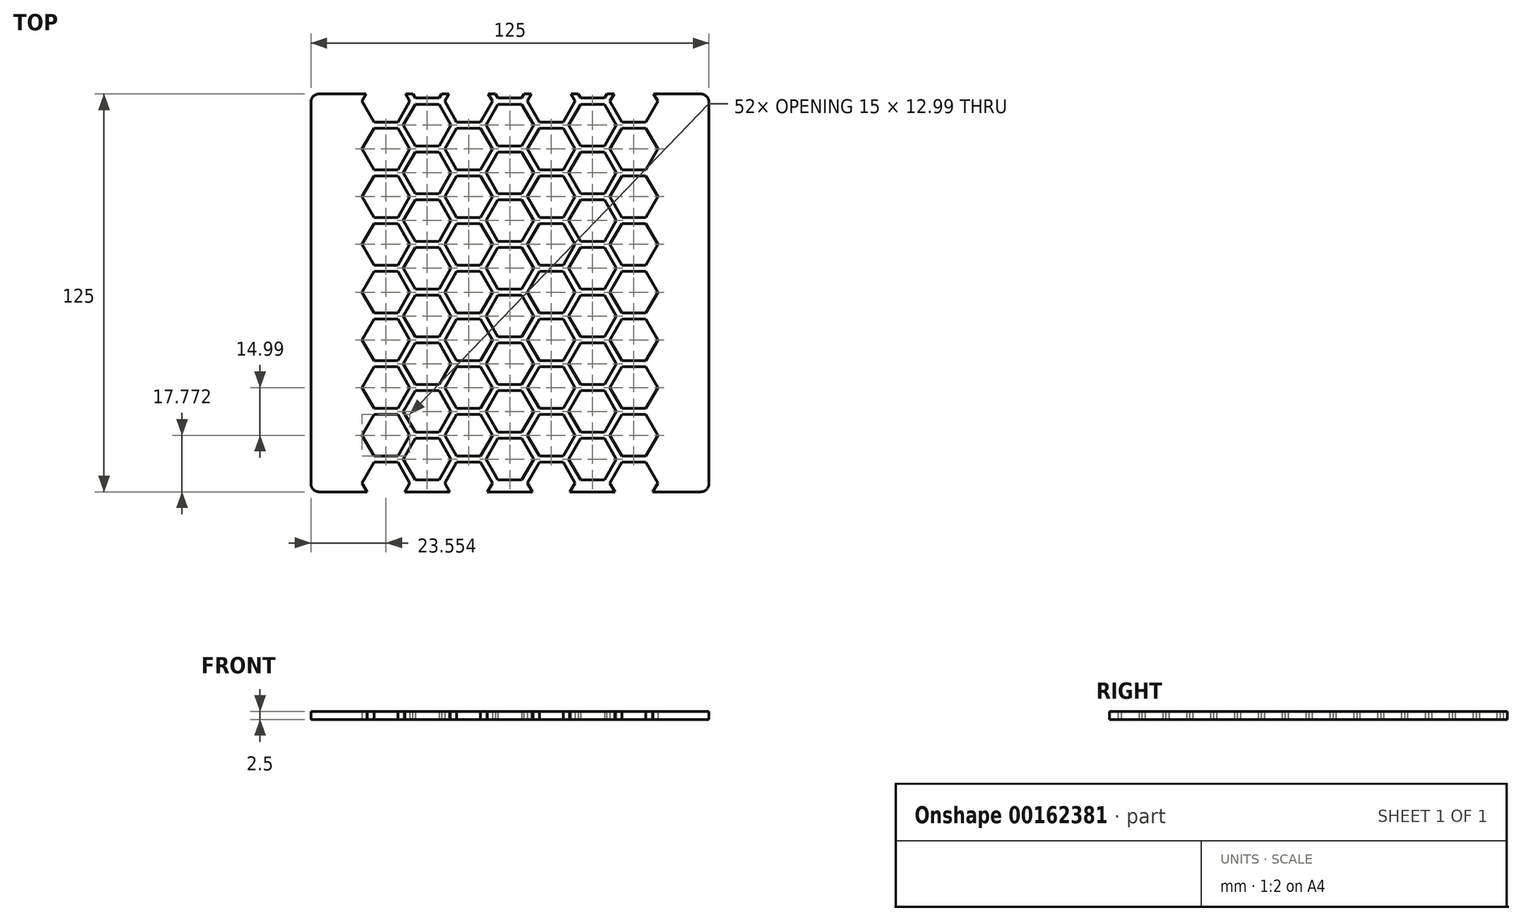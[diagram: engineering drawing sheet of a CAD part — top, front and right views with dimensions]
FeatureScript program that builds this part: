
annotation { "Feature Type Name" : "Feature", "Feature Type Description" : "" }
export const myFeature = defineFeature(function(context is Context, id is Id, definition is map)
    precondition{}
    {
        {
            var Q0;
            Q0=qCreatedBy(makeId("Top.planeOp"),FACE);
            var sketch = newSketch(context, id + "F0", { "sketchPlane" : qUnion([Q0])});
            skPoint(sketch, "E0.middle", {"position": v(0, 0) * mm});
            skLineSegment(sketch, "E1.bottom", {"start": v(60, 62.5) * mm, "end": v(-60, 62.5) * mm});
            skLineSegment(sketch, "E1.top", {"start": v(60, -62.5) * mm, "end": v(-60, -62.5) * mm});
            skLineSegment(sketch, "E1.left", {"start": v(62.5, 60) * mm, "end": v(62.5, -60) * mm});
            skLineSegment(sketch, "E1.right", {"start": v(-62.5, 60) * mm, "end": v(-62.5, -60) * mm});
            skArc(sketch, "E2", {"start": v(-60, 62.5) * mm, "mid": v(-61.77, 61.77) * mm, "end": v(-62.5, 60) * mm});
            skArc(sketch, "E3", {"start": v(62.5, 60) * mm, "mid": v(61.77, 61.77) * mm, "end": v(60, 62.5) * mm});
            skArc(sketch, "E4", {"start": v(60, -62.5) * mm, "mid": v(61.77, -61.77) * mm, "end": v(62.5, -60) * mm});
            skArc(sketch, "E5", {"start": v(-62.5, -60) * mm, "mid": v(-61.77, -61.77) * mm, "end": v(-60, -62.5) * mm});
            skLineSegment(sketch, "E6", {"start": v(0, 0) * mm, "end": v(0, 62.5) * mm, "construction": true});
            skLineSegment(sketch, "E7", {"start": v(0, 0) * mm, "end": v(0, -62.5) * mm, "construction": true});
            skSolve(sketch);
        }
        {
            var Q0;
            Q0=makeQuery(id+"F0.imprint","IMPRINT",FACE,{"disambiguationData":[TD([[makeQuery(id+"F0.imprint","IMPRINT",EDGE,{"derivedFrom":sQuery(id+"F0.wireOp",EDGE,"E1.bottom")}),1.0]])]});
            extrude(context, id + "F1", {"entities" : qUnion([Q0]), "offsetDistance" : 25 * mm, "depth" : 2.5 * mm});
        }
        {
            var Q0;
            Q0=qCreatedBy(makeId("Top.planeOp"),FACE);
            var sketch = newSketch(context, id + "F2", { "sketchPlane" : qUnion([Q0])});
            skCircle(sketch, "E8.cCircle", {"center": v(0, -52.22) * mm, "radius": 7.5 * mm, "construction": true});
            skLineSegment(sketch, "E8.0", {"start": v(7.5, -52.22) * mm, "end": v(3.75, -58.72) * mm});
            skLineSegment(sketch, "E8.1", {"start": v(3.75, -58.72) * mm, "end": v(-3.75, -58.72) * mm});
            skLineSegment(sketch, "E8.2", {"start": v(-3.75, -58.72) * mm, "end": v(-7.5, -52.22) * mm});
            skLineSegment(sketch, "E8.3", {"start": v(-7.5, -52.22) * mm, "end": v(-3.75, -45.73) * mm});
            skLineSegment(sketch, "E8.4", {"start": v(-3.75, -45.73) * mm, "end": v(3.75, -45.73) * mm});
            skLineSegment(sketch, "E8.5", {"start": v(3.75, -45.73) * mm, "end": v(7.5, -52.22) * mm});
            skCircle(sketch, "E9.cCircle", {"center": v(-12.98, -59.72) * mm, "radius": 7.5 * mm, "construction": true});
            skLineSegment(sketch, "E9.0", {"start": v(-16.73, -53.22) * mm, "end": v(-9.23, -53.22) * mm});
            skLineSegment(sketch, "E9.1", {"start": v(-9.23, -53.22) * mm, "end": v(-5.48, -59.72) * mm});
            skLineSegment(sketch, "E9.2", {"start": v(-5.48, -59.72) * mm, "end": v(-9.23, -66.21) * mm});
            skLineSegment(sketch, "E9.3", {"start": v(-9.23, -66.21) * mm, "end": v(-16.73, -66.21) * mm});
            skLineSegment(sketch, "E9.4", {"start": v(-16.73, -66.21) * mm, "end": v(-20.48, -59.72) * mm});
            skLineSegment(sketch, "E9.5", {"start": v(-20.48, -59.72) * mm, "end": v(-16.73, -53.22) * mm});
            skLineSegment(sketch, "E10", {"start": v(-12.98, -59.72) * mm, "end": v(0, -52.22) * mm, "construction": true});
            skCircle(sketch, "E11.MirrorC", {"center": v(12.98, -59.72) * mm, "radius": 7.5 * mm, "construction": true});
            skLineSegment(sketch, "E12.MirrorCS", {"start": v(5.48, -59.72) * mm, "end": v(9.23, -66.21) * mm});
            skLineSegment(sketch, "E13.MirrorCS", {"start": v(9.23, -66.21) * mm, "end": v(16.73, -66.21) * mm});
            skLineSegment(sketch, "E14.MirrorCS", {"start": v(16.73, -66.21) * mm, "end": v(20.48, -59.72) * mm});
            skLineSegment(sketch, "E15.MirrorCS", {"start": v(20.48, -59.72) * mm, "end": v(16.73, -53.22) * mm});
            skLineSegment(sketch, "E16.MirrorCS", {"start": v(16.73, -53.22) * mm, "end": v(9.23, -53.22) * mm});
            skLineSegment(sketch, "E17.MirrorCS", {"start": v(9.23, -53.22) * mm, "end": v(5.48, -59.72) * mm});
            skLineSegment(sketch, "E18.MirrorCS", {"start": v(12.98, -59.72) * mm, "end": v(0, -52.22) * mm, "construction": true});
            skLineSegment(sketch, "E19.1.0.0", {"start": v(38.95, -59.72) * mm, "end": v(25.96, -52.22) * mm, "construction": true});
            skLineSegment(sketch, "E19.1.0.1", {"start": v(29.71, -45.73) * mm, "end": v(33.46, -52.22) * mm});
            skLineSegment(sketch, "E19.1.0.2", {"start": v(12.98, -59.72) * mm, "end": v(25.96, -52.22) * mm, "construction": true});
            skLineSegment(sketch, "E19.1.0.3", {"start": v(22.21, -45.73) * mm, "end": v(29.71, -45.73) * mm});
            skLineSegment(sketch, "E19.1.0.4", {"start": v(42.7, -66.21) * mm, "end": v(46.45, -59.72) * mm});
            skLineSegment(sketch, "E19.1.0.5", {"start": v(46.45, -59.72) * mm, "end": v(42.7, -53.22) * mm});
            skLineSegment(sketch, "E19.1.0.6", {"start": v(31.45, -59.72) * mm, "end": v(35.2, -66.21) * mm});
            skCircle(sketch, "E19.1.0.7", {"center": v(25.96, -52.22) * mm, "radius": 7.5 * mm, "construction": true});
            skLineSegment(sketch, "E19.1.0.8", {"start": v(35.2, -53.22) * mm, "end": v(31.45, -59.72) * mm});
            skLineSegment(sketch, "E19.1.0.9", {"start": v(33.46, -52.22) * mm, "end": v(29.71, -58.72) * mm});
            skLineSegment(sketch, "E19.1.0.10", {"start": v(35.2, -66.21) * mm, "end": v(42.7, -66.21) * mm});
            skLineSegment(sketch, "E19.1.0.11", {"start": v(29.71, -58.72) * mm, "end": v(22.21, -58.72) * mm});
            skLineSegment(sketch, "E19.1.0.12", {"start": v(22.21, -58.72) * mm, "end": v(18.46, -52.22) * mm});
            skLineSegment(sketch, "E19.1.0.13", {"start": v(42.7, -53.22) * mm, "end": v(35.2, -53.22) * mm});
            skLineSegment(sketch, "E19.1.0.14", {"start": v(18.46, -52.22) * mm, "end": v(22.21, -45.73) * mm});
            skCircle(sketch, "E19.1.0.15", {"center": v(38.95, -59.72) * mm, "radius": 7.5 * mm, "construction": true});
            skLineSegment(sketch, "E19.direction1", {"start": v(-12.98, -59.72) * mm, "end": v(12.98, -59.72) * mm, "construction": true});
            skCircle(sketch, "E20.MirrorC", {"center": v(-25.96, -52.22) * mm, "radius": 7.5 * mm, "construction": true});
            skLineSegment(sketch, "E21.MirrorCS", {"start": v(-35.2, -66.21) * mm, "end": v(-42.7, -66.21) * mm});
            skLineSegment(sketch, "E22.MirrorCS", {"start": v(-12.98, -59.72) * mm, "end": v(-25.96, -52.22) * mm, "construction": true});
            skLineSegment(sketch, "E23.MirrorCS", {"start": v(-38.95, -59.72) * mm, "end": v(-25.96, -52.22) * mm, "construction": true});
            skLineSegment(sketch, "E24.MirrorCS", {"start": v(-46.45, -59.72) * mm, "end": v(-42.7, -53.22) * mm});
            skCircle(sketch, "E25.MirrorC", {"center": v(-38.95, -59.72) * mm, "radius": 7.5 * mm, "construction": true});
            skLineSegment(sketch, "E26.MirrorCS", {"start": v(-35.2, -53.22) * mm, "end": v(-31.45, -59.72) * mm});
            skLineSegment(sketch, "E27.MirrorCS", {"start": v(-29.71, -58.72) * mm, "end": v(-22.21, -58.72) * mm});
            skLineSegment(sketch, "E28.MirrorCS", {"start": v(-22.21, -45.73) * mm, "end": v(-29.71, -45.73) * mm});
            skLineSegment(sketch, "E29.MirrorCS", {"start": v(-22.21, -58.72) * mm, "end": v(-18.46, -52.22) * mm});
            skLineSegment(sketch, "E30.MirrorCS", {"start": v(-18.46, -52.22) * mm, "end": v(-22.21, -45.73) * mm});
            skLineSegment(sketch, "E31.MirrorCS", {"start": v(-31.45, -59.72) * mm, "end": v(-35.2, -66.21) * mm});
            skLineSegment(sketch, "E32.MirrorCS", {"start": v(-42.7, -66.21) * mm, "end": v(-46.45, -59.72) * mm});
            skLineSegment(sketch, "E33.MirrorCS", {"start": v(-33.46, -52.22) * mm, "end": v(-29.71, -58.72) * mm});
            skLineSegment(sketch, "E34.MirrorCS", {"start": v(-29.71, -45.73) * mm, "end": v(-33.46, -52.22) * mm});
            skLineSegment(sketch, "E35.MirrorCS", {"start": v(-42.7, -53.22) * mm, "end": v(-35.2, -53.22) * mm});
            skLineSegment(sketch, "E36.0.1.0", {"start": v(-3.75, -30.74) * mm, "end": v(3.75, -30.74) * mm});
            skLineSegment(sketch, "E36.0.1.1", {"start": v(-7.5, -37.23) * mm, "end": v(-3.75, -30.74) * mm});
            skLineSegment(sketch, "E36.0.1.2", {"start": v(7.5, -37.23) * mm, "end": v(3.75, -43.73) * mm});
            skLineSegment(sketch, "E36.0.1.3", {"start": v(-20.48, -44.73) * mm, "end": v(-16.73, -38.23) * mm});
            skCircle(sketch, "E36.0.1.4", {"center": v(-25.96, -37.23) * mm, "radius": 7.5 * mm, "construction": true});
            skLineSegment(sketch, "E36.0.1.5", {"start": v(35.2, -38.23) * mm, "end": v(31.45, -44.73) * mm});
            skLineSegment(sketch, "E36.0.1.6", {"start": v(12.98, -44.73) * mm, "end": v(0, -37.23) * mm, "construction": true});
            skCircle(sketch, "E36.0.1.7", {"center": v(38.95, -44.73) * mm, "radius": 7.5 * mm, "construction": true});
            skLineSegment(sketch, "E36.0.1.8", {"start": v(-12.98, -44.73) * mm, "end": v(0, -37.23) * mm, "construction": true});
            skLineSegment(sketch, "E36.0.1.9", {"start": v(9.23, -38.23) * mm, "end": v(5.48, -44.73) * mm});
            skCircle(sketch, "E36.0.1.10", {"center": v(-38.95, -44.73) * mm, "radius": 7.5 * mm, "construction": true});
            skLineSegment(sketch, "E36.0.1.11", {"start": v(-5.48, -44.73) * mm, "end": v(-9.23, -51.22) * mm});
            skLineSegment(sketch, "E36.0.1.12", {"start": v(33.46, -37.23) * mm, "end": v(29.71, -43.73) * mm});
            skLineSegment(sketch, "E36.0.1.13", {"start": v(35.2, -51.22) * mm, "end": v(42.7, -51.22) * mm});
            skLineSegment(sketch, "E36.0.1.14", {"start": v(29.71, -43.73) * mm, "end": v(22.21, -43.73) * mm});
            skLineSegment(sketch, "E36.0.1.15", {"start": v(12.98, -44.73) * mm, "end": v(25.96, -37.23) * mm, "construction": true});
            skCircle(sketch, "E36.0.1.16", {"center": v(0, -37.23) * mm, "radius": 7.5 * mm, "construction": true});
            skCircle(sketch, "E36.0.1.17", {"center": v(-12.98, -44.73) * mm, "radius": 7.5 * mm, "construction": true});
            skLineSegment(sketch, "E36.0.1.18", {"start": v(-16.73, -38.23) * mm, "end": v(-9.23, -38.23) * mm});
            skLineSegment(sketch, "E36.0.1.19", {"start": v(-3.75, -43.73) * mm, "end": v(-7.5, -37.23) * mm});
            skLineSegment(sketch, "E36.0.1.20", {"start": v(3.75, -30.74) * mm, "end": v(7.5, -37.23) * mm});
            skLineSegment(sketch, "E36.0.1.21", {"start": v(-22.21, -43.73) * mm, "end": v(-18.46, -37.23) * mm});
            skLineSegment(sketch, "E36.0.1.22", {"start": v(-31.45, -44.73) * mm, "end": v(-35.2, -51.22) * mm});
            skLineSegment(sketch, "E36.0.1.23", {"start": v(16.73, -38.23) * mm, "end": v(9.23, -38.23) * mm});
            skLineSegment(sketch, "E36.0.1.24", {"start": v(29.71, -30.74) * mm, "end": v(33.46, -37.23) * mm});
            skLineSegment(sketch, "E36.0.1.25", {"start": v(46.45, -44.73) * mm, "end": v(42.7, -38.23) * mm});
            skLineSegment(sketch, "E36.0.1.26", {"start": v(42.7, -51.22) * mm, "end": v(46.45, -44.73) * mm});
            skLineSegment(sketch, "E36.0.1.27", {"start": v(5.48, -44.73) * mm, "end": v(9.23, -51.22) * mm});
            skLineSegment(sketch, "E36.0.1.28", {"start": v(-46.45, -44.73) * mm, "end": v(-42.7, -38.23) * mm});
            skLineSegment(sketch, "E36.0.1.29", {"start": v(31.45, -44.73) * mm, "end": v(35.2, -51.22) * mm});
            skLineSegment(sketch, "E36.0.1.30", {"start": v(16.73, -51.22) * mm, "end": v(20.48, -44.73) * mm});
            skLineSegment(sketch, "E36.0.1.31", {"start": v(-16.73, -51.22) * mm, "end": v(-20.48, -44.73) * mm});
            skLineSegment(sketch, "E36.0.1.32", {"start": v(-29.71, -43.73) * mm, "end": v(-22.21, -43.73) * mm});
            skLineSegment(sketch, "E36.0.1.33", {"start": v(20.48, -44.73) * mm, "end": v(16.73, -38.23) * mm});
            skLineSegment(sketch, "E36.0.1.34", {"start": v(-12.98, -44.73) * mm, "end": v(-25.96, -37.23) * mm, "construction": true});
            skLineSegment(sketch, "E36.0.1.35", {"start": v(-18.46, -37.23) * mm, "end": v(-22.21, -30.74) * mm});
            skLineSegment(sketch, "E36.0.1.36", {"start": v(42.7, -38.23) * mm, "end": v(35.2, -38.23) * mm});
            skLineSegment(sketch, "E36.0.1.37", {"start": v(-22.21, -30.74) * mm, "end": v(-29.71, -30.74) * mm});
            skLineSegment(sketch, "E36.0.1.38", {"start": v(-35.2, -38.23) * mm, "end": v(-31.45, -44.73) * mm});
            skLineSegment(sketch, "E36.0.1.39", {"start": v(-9.23, -51.22) * mm, "end": v(-16.73, -51.22) * mm});
            skLineSegment(sketch, "E36.0.1.40", {"start": v(22.21, -30.74) * mm, "end": v(29.71, -30.74) * mm});
            skLineSegment(sketch, "E36.0.1.41", {"start": v(22.21, -43.73) * mm, "end": v(18.46, -37.23) * mm});
            skLineSegment(sketch, "E36.0.1.42", {"start": v(3.75, -43.73) * mm, "end": v(-3.75, -43.73) * mm});
            skLineSegment(sketch, "E36.0.1.43", {"start": v(38.95, -44.73) * mm, "end": v(25.96, -37.23) * mm, "construction": true});
            skCircle(sketch, "E36.0.1.44", {"center": v(12.98, -44.73) * mm, "radius": 7.5 * mm, "construction": true});
            skLineSegment(sketch, "E36.0.1.45", {"start": v(-29.71, -30.74) * mm, "end": v(-33.46, -37.23) * mm});
            skCircle(sketch, "E36.0.1.46", {"center": v(25.96, -37.23) * mm, "radius": 7.5 * mm, "construction": true});
            skLineSegment(sketch, "E36.0.1.47", {"start": v(18.46, -37.23) * mm, "end": v(22.21, -30.74) * mm});
            skLineSegment(sketch, "E36.0.1.48", {"start": v(-35.2, -51.22) * mm, "end": v(-42.7, -51.22) * mm});
            skLineSegment(sketch, "E36.0.1.49", {"start": v(9.23, -51.22) * mm, "end": v(16.73, -51.22) * mm});
            skLineSegment(sketch, "E36.0.1.50", {"start": v(-33.46, -37.23) * mm, "end": v(-29.71, -43.73) * mm});
            skLineSegment(sketch, "E36.0.1.51", {"start": v(-42.7, -38.23) * mm, "end": v(-35.2, -38.23) * mm});
            skLineSegment(sketch, "E36.0.1.52", {"start": v(-42.7, -51.22) * mm, "end": v(-46.45, -44.73) * mm});
            skLineSegment(sketch, "E36.0.1.53", {"start": v(-38.95, -44.73) * mm, "end": v(-25.96, -37.23) * mm, "construction": true});
            skLineSegment(sketch, "E36.0.1.54", {"start": v(-12.98, -44.73) * mm, "end": v(12.98, -44.73) * mm, "construction": true});
            skLineSegment(sketch, "E36.0.1.55", {"start": v(-9.23, -38.23) * mm, "end": v(-5.48, -44.73) * mm});
            skLineSegment(sketch, "E36.0.2.0", {"start": v(-3.75, -15.75) * mm, "end": v(3.75, -15.75) * mm});
            skLineSegment(sketch, "E36.0.2.1", {"start": v(-7.5, -22.24) * mm, "end": v(-3.75, -15.75) * mm});
            skLineSegment(sketch, "E36.0.2.2", {"start": v(7.5, -22.24) * mm, "end": v(3.75, -28.74) * mm});
            skLineSegment(sketch, "E36.0.2.3", {"start": v(-20.48, -29.74) * mm, "end": v(-16.73, -23.24) * mm});
            skCircle(sketch, "E36.0.2.4", {"center": v(-25.96, -22.24) * mm, "radius": 7.5 * mm, "construction": true});
            skLineSegment(sketch, "E36.0.2.5", {"start": v(35.2, -23.24) * mm, "end": v(31.45, -29.74) * mm});
            skLineSegment(sketch, "E36.0.2.6", {"start": v(12.98, -29.74) * mm, "end": v(0, -22.24) * mm, "construction": true});
            skCircle(sketch, "E36.0.2.7", {"center": v(38.95, -29.74) * mm, "radius": 7.5 * mm, "construction": true});
            skLineSegment(sketch, "E36.0.2.8", {"start": v(-12.98, -29.74) * mm, "end": v(0, -22.24) * mm, "construction": true});
            skLineSegment(sketch, "E36.0.2.9", {"start": v(9.23, -23.24) * mm, "end": v(5.48, -29.74) * mm});
            skCircle(sketch, "E36.0.2.10", {"center": v(-38.95, -29.74) * mm, "radius": 7.5 * mm, "construction": true});
            skLineSegment(sketch, "E36.0.2.11", {"start": v(-5.48, -29.74) * mm, "end": v(-9.23, -36.23) * mm});
            skLineSegment(sketch, "E36.0.2.12", {"start": v(33.46, -22.24) * mm, "end": v(29.71, -28.74) * mm});
            skLineSegment(sketch, "E36.0.2.13", {"start": v(35.2, -36.23) * mm, "end": v(42.7, -36.23) * mm});
            skLineSegment(sketch, "E36.0.2.14", {"start": v(29.71, -28.74) * mm, "end": v(22.21, -28.74) * mm});
            skLineSegment(sketch, "E36.0.2.15", {"start": v(12.98, -29.74) * mm, "end": v(25.96, -22.24) * mm, "construction": true});
            skCircle(sketch, "E36.0.2.16", {"center": v(0, -22.24) * mm, "radius": 7.5 * mm, "construction": true});
            skCircle(sketch, "E36.0.2.17", {"center": v(-12.98, -29.74) * mm, "radius": 7.5 * mm, "construction": true});
            skLineSegment(sketch, "E36.0.2.18", {"start": v(-16.73, -23.24) * mm, "end": v(-9.23, -23.24) * mm});
            skLineSegment(sketch, "E36.0.2.19", {"start": v(-3.75, -28.74) * mm, "end": v(-7.5, -22.24) * mm});
            skLineSegment(sketch, "E36.0.2.20", {"start": v(3.75, -15.75) * mm, "end": v(7.5, -22.24) * mm});
            skLineSegment(sketch, "E36.0.2.21", {"start": v(-22.21, -28.74) * mm, "end": v(-18.46, -22.24) * mm});
            skLineSegment(sketch, "E36.0.2.22", {"start": v(-31.45, -29.74) * mm, "end": v(-35.2, -36.23) * mm});
            skLineSegment(sketch, "E36.0.2.23", {"start": v(16.73, -23.24) * mm, "end": v(9.23, -23.24) * mm});
            skLineSegment(sketch, "E36.0.2.24", {"start": v(29.71, -15.75) * mm, "end": v(33.46, -22.24) * mm});
            skLineSegment(sketch, "E36.0.2.25", {"start": v(46.45, -29.74) * mm, "end": v(42.7, -23.24) * mm});
            skLineSegment(sketch, "E36.0.2.26", {"start": v(42.7, -36.23) * mm, "end": v(46.45, -29.74) * mm});
            skLineSegment(sketch, "E36.0.2.27", {"start": v(5.48, -29.74) * mm, "end": v(9.23, -36.23) * mm});
            skLineSegment(sketch, "E36.0.2.28", {"start": v(-46.45, -29.74) * mm, "end": v(-42.7, -23.24) * mm});
            skLineSegment(sketch, "E36.0.2.29", {"start": v(31.45, -29.74) * mm, "end": v(35.2, -36.23) * mm});
            skLineSegment(sketch, "E36.0.2.30", {"start": v(16.73, -36.23) * mm, "end": v(20.48, -29.74) * mm});
            skLineSegment(sketch, "E36.0.2.31", {"start": v(-16.73, -36.23) * mm, "end": v(-20.48, -29.74) * mm});
            skLineSegment(sketch, "E36.0.2.32", {"start": v(-29.71, -28.74) * mm, "end": v(-22.21, -28.74) * mm});
            skLineSegment(sketch, "E36.0.2.33", {"start": v(20.48, -29.74) * mm, "end": v(16.73, -23.24) * mm});
            skLineSegment(sketch, "E36.0.2.34", {"start": v(-12.98, -29.74) * mm, "end": v(-25.96, -22.24) * mm, "construction": true});
            skLineSegment(sketch, "E36.0.2.35", {"start": v(-18.46, -22.24) * mm, "end": v(-22.21, -15.75) * mm});
            skLineSegment(sketch, "E36.0.2.36", {"start": v(42.7, -23.24) * mm, "end": v(35.2, -23.24) * mm});
            skLineSegment(sketch, "E36.0.2.37", {"start": v(-22.21, -15.75) * mm, "end": v(-29.71, -15.75) * mm});
            skLineSegment(sketch, "E36.0.2.38", {"start": v(-35.2, -23.24) * mm, "end": v(-31.45, -29.74) * mm});
            skLineSegment(sketch, "E36.0.2.39", {"start": v(-9.23, -36.23) * mm, "end": v(-16.73, -36.23) * mm});
            skLineSegment(sketch, "E36.0.2.40", {"start": v(22.21, -15.75) * mm, "end": v(29.71, -15.75) * mm});
            skLineSegment(sketch, "E36.0.2.41", {"start": v(22.21, -28.74) * mm, "end": v(18.46, -22.24) * mm});
            skLineSegment(sketch, "E36.0.2.42", {"start": v(3.75, -28.74) * mm, "end": v(-3.75, -28.74) * mm});
            skLineSegment(sketch, "E36.0.2.43", {"start": v(38.95, -29.74) * mm, "end": v(25.96, -22.24) * mm, "construction": true});
            skCircle(sketch, "E36.0.2.44", {"center": v(12.98, -29.74) * mm, "radius": 7.5 * mm, "construction": true});
            skLineSegment(sketch, "E36.0.2.45", {"start": v(-29.71, -15.75) * mm, "end": v(-33.46, -22.24) * mm});
            skCircle(sketch, "E36.0.2.46", {"center": v(25.96, -22.24) * mm, "radius": 7.5 * mm, "construction": true});
            skLineSegment(sketch, "E36.0.2.47", {"start": v(18.46, -22.24) * mm, "end": v(22.21, -15.75) * mm});
            skLineSegment(sketch, "E36.0.2.48", {"start": v(-35.2, -36.23) * mm, "end": v(-42.7, -36.23) * mm});
            skLineSegment(sketch, "E36.0.2.49", {"start": v(9.23, -36.23) * mm, "end": v(16.73, -36.23) * mm});
            skLineSegment(sketch, "E36.0.2.50", {"start": v(-33.46, -22.24) * mm, "end": v(-29.71, -28.74) * mm});
            skLineSegment(sketch, "E36.0.2.51", {"start": v(-42.7, -23.24) * mm, "end": v(-35.2, -23.24) * mm});
            skLineSegment(sketch, "E36.0.2.52", {"start": v(-42.7, -36.23) * mm, "end": v(-46.45, -29.74) * mm});
            skLineSegment(sketch, "E36.0.2.53", {"start": v(-38.95, -29.74) * mm, "end": v(-25.96, -22.24) * mm, "construction": true});
            skLineSegment(sketch, "E36.0.2.54", {"start": v(-12.98, -29.74) * mm, "end": v(12.98, -29.74) * mm, "construction": true});
            skLineSegment(sketch, "E36.0.2.55", {"start": v(-9.23, -23.24) * mm, "end": v(-5.48, -29.74) * mm});
            skLineSegment(sketch, "E36.0.3.0", {"start": v(-3.75, -0.76) * mm, "end": v(3.75, -0.76) * mm});
            skLineSegment(sketch, "E36.0.3.1", {"start": v(-7.5, -7.25) * mm, "end": v(-3.75, -0.76) * mm});
            skLineSegment(sketch, "E36.0.3.2", {"start": v(7.5, -7.25) * mm, "end": v(3.75, -13.75) * mm});
            skLineSegment(sketch, "E36.0.3.3", {"start": v(-20.48, -14.75) * mm, "end": v(-16.73, -8.25) * mm});
            skCircle(sketch, "E36.0.3.4", {"center": v(-25.96, -7.25) * mm, "radius": 7.5 * mm, "construction": true});
            skLineSegment(sketch, "E36.0.3.5", {"start": v(35.2, -8.25) * mm, "end": v(31.45, -14.75) * mm});
            skLineSegment(sketch, "E36.0.3.6", {"start": v(12.98, -14.75) * mm, "end": v(0, -7.25) * mm, "construction": true});
            skCircle(sketch, "E36.0.3.7", {"center": v(38.95, -14.75) * mm, "radius": 7.5 * mm, "construction": true});
            skLineSegment(sketch, "E36.0.3.8", {"start": v(-12.98, -14.75) * mm, "end": v(0, -7.25) * mm, "construction": true});
            skLineSegment(sketch, "E36.0.3.9", {"start": v(9.23, -8.25) * mm, "end": v(5.48, -14.75) * mm});
            skCircle(sketch, "E36.0.3.10", {"center": v(-38.95, -14.75) * mm, "radius": 7.5 * mm, "construction": true});
            skLineSegment(sketch, "E36.0.3.11", {"start": v(-5.48, -14.75) * mm, "end": v(-9.23, -21.24) * mm});
            skLineSegment(sketch, "E36.0.3.12", {"start": v(33.46, -7.25) * mm, "end": v(29.71, -13.75) * mm});
            skLineSegment(sketch, "E36.0.3.13", {"start": v(35.2, -21.24) * mm, "end": v(42.7, -21.24) * mm});
            skLineSegment(sketch, "E36.0.3.14", {"start": v(29.71, -13.75) * mm, "end": v(22.21, -13.75) * mm});
            skLineSegment(sketch, "E36.0.3.15", {"start": v(12.98, -14.75) * mm, "end": v(25.96, -7.25) * mm, "construction": true});
            skCircle(sketch, "E36.0.3.16", {"center": v(0, -7.25) * mm, "radius": 7.5 * mm, "construction": true});
            skCircle(sketch, "E36.0.3.17", {"center": v(-12.98, -14.75) * mm, "radius": 7.5 * mm, "construction": true});
            skLineSegment(sketch, "E36.0.3.18", {"start": v(-16.73, -8.25) * mm, "end": v(-9.23, -8.25) * mm});
            skLineSegment(sketch, "E36.0.3.19", {"start": v(-3.75, -13.75) * mm, "end": v(-7.5, -7.25) * mm});
            skLineSegment(sketch, "E36.0.3.20", {"start": v(3.75, -0.76) * mm, "end": v(7.5, -7.25) * mm});
            skLineSegment(sketch, "E36.0.3.21", {"start": v(-22.21, -13.75) * mm, "end": v(-18.46, -7.25) * mm});
            skLineSegment(sketch, "E36.0.3.22", {"start": v(-31.45, -14.75) * mm, "end": v(-35.2, -21.24) * mm});
            skLineSegment(sketch, "E36.0.3.23", {"start": v(16.73, -8.25) * mm, "end": v(9.23, -8.25) * mm});
            skLineSegment(sketch, "E36.0.3.24", {"start": v(29.71, -0.76) * mm, "end": v(33.46, -7.25) * mm});
            skLineSegment(sketch, "E36.0.3.25", {"start": v(46.45, -14.75) * mm, "end": v(42.7, -8.25) * mm});
            skLineSegment(sketch, "E36.0.3.26", {"start": v(42.7, -21.24) * mm, "end": v(46.45, -14.75) * mm});
            skLineSegment(sketch, "E36.0.3.27", {"start": v(5.48, -14.75) * mm, "end": v(9.23, -21.24) * mm});
            skLineSegment(sketch, "E36.0.3.28", {"start": v(-46.45, -14.75) * mm, "end": v(-42.7, -8.25) * mm});
            skLineSegment(sketch, "E36.0.3.29", {"start": v(31.45, -14.75) * mm, "end": v(35.2, -21.24) * mm});
            skLineSegment(sketch, "E36.0.3.30", {"start": v(16.73, -21.24) * mm, "end": v(20.48, -14.75) * mm});
            skLineSegment(sketch, "E36.0.3.31", {"start": v(-16.73, -21.24) * mm, "end": v(-20.48, -14.75) * mm});
            skLineSegment(sketch, "E36.0.3.32", {"start": v(-29.71, -13.75) * mm, "end": v(-22.21, -13.75) * mm});
            skLineSegment(sketch, "E36.0.3.33", {"start": v(20.48, -14.75) * mm, "end": v(16.73, -8.25) * mm});
            skLineSegment(sketch, "E36.0.3.34", {"start": v(-12.98, -14.75) * mm, "end": v(-25.96, -7.25) * mm, "construction": true});
            skLineSegment(sketch, "E36.0.3.35", {"start": v(-18.46, -7.25) * mm, "end": v(-22.21, -0.76) * mm});
            skLineSegment(sketch, "E36.0.3.36", {"start": v(42.7, -8.25) * mm, "end": v(35.2, -8.25) * mm});
            skLineSegment(sketch, "E36.0.3.37", {"start": v(-22.21, -0.76) * mm, "end": v(-29.71, -0.76) * mm});
            skLineSegment(sketch, "E36.0.3.38", {"start": v(-35.2, -8.25) * mm, "end": v(-31.45, -14.75) * mm});
            skLineSegment(sketch, "E36.0.3.39", {"start": v(-9.23, -21.24) * mm, "end": v(-16.73, -21.24) * mm});
            skLineSegment(sketch, "E36.0.3.40", {"start": v(22.21, -0.76) * mm, "end": v(29.71, -0.76) * mm});
            skLineSegment(sketch, "E36.0.3.41", {"start": v(22.21, -13.75) * mm, "end": v(18.46, -7.25) * mm});
            skLineSegment(sketch, "E36.0.3.42", {"start": v(3.75, -13.75) * mm, "end": v(-3.75, -13.75) * mm});
            skLineSegment(sketch, "E36.0.3.43", {"start": v(38.95, -14.75) * mm, "end": v(25.96, -7.25) * mm, "construction": true});
            skCircle(sketch, "E36.0.3.44", {"center": v(12.98, -14.75) * mm, "radius": 7.5 * mm, "construction": true});
            skLineSegment(sketch, "E36.0.3.45", {"start": v(-29.71, -0.76) * mm, "end": v(-33.46, -7.25) * mm});
            skCircle(sketch, "E36.0.3.46", {"center": v(25.96, -7.25) * mm, "radius": 7.5 * mm, "construction": true});
            skLineSegment(sketch, "E36.0.3.47", {"start": v(18.46, -7.25) * mm, "end": v(22.21, -0.76) * mm});
            skLineSegment(sketch, "E36.0.3.48", {"start": v(-35.2, -21.24) * mm, "end": v(-42.7, -21.24) * mm});
            skLineSegment(sketch, "E36.0.3.49", {"start": v(9.23, -21.24) * mm, "end": v(16.73, -21.24) * mm});
            skLineSegment(sketch, "E36.0.3.50", {"start": v(-33.46, -7.25) * mm, "end": v(-29.71, -13.75) * mm});
            skLineSegment(sketch, "E36.0.3.51", {"start": v(-42.7, -8.25) * mm, "end": v(-35.2, -8.25) * mm});
            skLineSegment(sketch, "E36.0.3.52", {"start": v(-42.7, -21.24) * mm, "end": v(-46.45, -14.75) * mm});
            skLineSegment(sketch, "E36.0.3.53", {"start": v(-38.95, -14.75) * mm, "end": v(-25.96, -7.25) * mm, "construction": true});
            skLineSegment(sketch, "E36.0.3.54", {"start": v(-12.98, -14.75) * mm, "end": v(12.98, -14.75) * mm, "construction": true});
            skLineSegment(sketch, "E36.0.3.55", {"start": v(-9.23, -8.25) * mm, "end": v(-5.48, -14.75) * mm});
            skLineSegment(sketch, "E36.0.4.0", {"start": v(-3.75, 14.23) * mm, "end": v(3.75, 14.23) * mm});
            skLineSegment(sketch, "E36.0.4.1", {"start": v(-7.5, 7.74) * mm, "end": v(-3.75, 14.23) * mm});
            skLineSegment(sketch, "E36.0.4.2", {"start": v(7.5, 7.74) * mm, "end": v(3.75, 1.24) * mm});
            skLineSegment(sketch, "E36.0.4.3", {"start": v(-20.48, 0.24) * mm, "end": v(-16.73, 6.74) * mm});
            skCircle(sketch, "E36.0.4.4", {"center": v(-25.96, 7.74) * mm, "radius": 7.5 * mm, "construction": true});
            skLineSegment(sketch, "E36.0.4.5", {"start": v(35.2, 6.74) * mm, "end": v(31.45, 0.24) * mm});
            skLineSegment(sketch, "E36.0.4.6", {"start": v(12.98, 0.24) * mm, "end": v(0, 7.74) * mm, "construction": true});
            skCircle(sketch, "E36.0.4.7", {"center": v(38.95, 0.24) * mm, "radius": 7.5 * mm, "construction": true});
            skLineSegment(sketch, "E36.0.4.8", {"start": v(-12.98, 0.24) * mm, "end": v(0, 7.74) * mm, "construction": true});
            skLineSegment(sketch, "E36.0.4.9", {"start": v(9.23, 6.74) * mm, "end": v(5.48, 0.24) * mm});
            skCircle(sketch, "E36.0.4.10", {"center": v(-38.95, 0.24) * mm, "radius": 7.5 * mm, "construction": true});
            skLineSegment(sketch, "E36.0.4.11", {"start": v(-5.48, 0.24) * mm, "end": v(-9.23, -6.25) * mm});
            skLineSegment(sketch, "E36.0.4.12", {"start": v(33.46, 7.74) * mm, "end": v(29.71, 1.24) * mm});
            skLineSegment(sketch, "E36.0.4.13", {"start": v(35.2, -6.25) * mm, "end": v(42.7, -6.25) * mm});
            skLineSegment(sketch, "E36.0.4.14", {"start": v(29.71, 1.24) * mm, "end": v(22.21, 1.24) * mm});
            skLineSegment(sketch, "E36.0.4.15", {"start": v(12.98, 0.24) * mm, "end": v(25.96, 7.74) * mm, "construction": true});
            skCircle(sketch, "E36.0.4.16", {"center": v(0, 7.74) * mm, "radius": 7.5 * mm, "construction": true});
            skCircle(sketch, "E36.0.4.17", {"center": v(-12.98, 0.24) * mm, "radius": 7.5 * mm, "construction": true});
            skLineSegment(sketch, "E36.0.4.18", {"start": v(-16.73, 6.74) * mm, "end": v(-9.23, 6.74) * mm});
            skLineSegment(sketch, "E36.0.4.19", {"start": v(-3.75, 1.24) * mm, "end": v(-7.5, 7.74) * mm});
            skLineSegment(sketch, "E36.0.4.20", {"start": v(3.75, 14.23) * mm, "end": v(7.5, 7.74) * mm});
            skLineSegment(sketch, "E36.0.4.21", {"start": v(-22.21, 1.24) * mm, "end": v(-18.46, 7.74) * mm});
            skLineSegment(sketch, "E36.0.4.22", {"start": v(-31.45, 0.24) * mm, "end": v(-35.2, -6.25) * mm});
            skLineSegment(sketch, "E36.0.4.23", {"start": v(16.73, 6.74) * mm, "end": v(9.23, 6.74) * mm});
            skLineSegment(sketch, "E36.0.4.24", {"start": v(29.71, 14.23) * mm, "end": v(33.46, 7.74) * mm});
            skLineSegment(sketch, "E36.0.4.25", {"start": v(46.45, 0.24) * mm, "end": v(42.7, 6.74) * mm});
            skLineSegment(sketch, "E36.0.4.26", {"start": v(42.7, -6.25) * mm, "end": v(46.45, 0.24) * mm});
            skLineSegment(sketch, "E36.0.4.27", {"start": v(5.48, 0.24) * mm, "end": v(9.23, -6.25) * mm});
            skLineSegment(sketch, "E36.0.4.28", {"start": v(-46.45, 0.24) * mm, "end": v(-42.7, 6.74) * mm});
            skLineSegment(sketch, "E36.0.4.29", {"start": v(31.45, 0.24) * mm, "end": v(35.2, -6.25) * mm});
            skLineSegment(sketch, "E36.0.4.30", {"start": v(16.73, -6.25) * mm, "end": v(20.48, 0.24) * mm});
            skLineSegment(sketch, "E36.0.4.31", {"start": v(-16.73, -6.25) * mm, "end": v(-20.48, 0.24) * mm});
            skLineSegment(sketch, "E36.0.4.32", {"start": v(-29.71, 1.24) * mm, "end": v(-22.21, 1.24) * mm});
            skLineSegment(sketch, "E36.0.4.33", {"start": v(20.48, 0.24) * mm, "end": v(16.73, 6.74) * mm});
            skLineSegment(sketch, "E36.0.4.34", {"start": v(-12.98, 0.24) * mm, "end": v(-25.96, 7.74) * mm, "construction": true});
            skLineSegment(sketch, "E36.0.4.35", {"start": v(-18.46, 7.74) * mm, "end": v(-22.21, 14.23) * mm});
            skLineSegment(sketch, "E36.0.4.36", {"start": v(42.7, 6.74) * mm, "end": v(35.2, 6.74) * mm});
            skLineSegment(sketch, "E36.0.4.37", {"start": v(-22.21, 14.23) * mm, "end": v(-29.71, 14.23) * mm});
            skLineSegment(sketch, "E36.0.4.38", {"start": v(-35.2, 6.74) * mm, "end": v(-31.45, 0.24) * mm});
            skLineSegment(sketch, "E36.0.4.39", {"start": v(-9.23, -6.25) * mm, "end": v(-16.73, -6.25) * mm});
            skLineSegment(sketch, "E36.0.4.40", {"start": v(22.21, 14.23) * mm, "end": v(29.71, 14.23) * mm});
            skLineSegment(sketch, "E36.0.4.41", {"start": v(22.21, 1.24) * mm, "end": v(18.46, 7.74) * mm});
            skLineSegment(sketch, "E36.0.4.42", {"start": v(3.75, 1.24) * mm, "end": v(-3.75, 1.24) * mm});
            skLineSegment(sketch, "E36.0.4.43", {"start": v(38.95, 0.24) * mm, "end": v(25.96, 7.74) * mm, "construction": true});
            skCircle(sketch, "E36.0.4.44", {"center": v(12.98, 0.24) * mm, "radius": 7.5 * mm, "construction": true});
            skLineSegment(sketch, "E36.0.4.45", {"start": v(-29.71, 14.23) * mm, "end": v(-33.46, 7.74) * mm});
            skCircle(sketch, "E36.0.4.46", {"center": v(25.96, 7.74) * mm, "radius": 7.5 * mm, "construction": true});
            skLineSegment(sketch, "E36.0.4.47", {"start": v(18.46, 7.74) * mm, "end": v(22.21, 14.23) * mm});
            skLineSegment(sketch, "E36.0.4.48", {"start": v(-35.2, -6.25) * mm, "end": v(-42.7, -6.25) * mm});
            skLineSegment(sketch, "E36.0.4.49", {"start": v(9.23, -6.25) * mm, "end": v(16.73, -6.25) * mm});
            skLineSegment(sketch, "E36.0.4.50", {"start": v(-33.46, 7.74) * mm, "end": v(-29.71, 1.24) * mm});
            skLineSegment(sketch, "E36.0.4.51", {"start": v(-42.7, 6.74) * mm, "end": v(-35.2, 6.74) * mm});
            skLineSegment(sketch, "E36.0.4.52", {"start": v(-42.7, -6.25) * mm, "end": v(-46.45, 0.24) * mm});
            skLineSegment(sketch, "E36.0.4.53", {"start": v(-38.95, 0.24) * mm, "end": v(-25.96, 7.74) * mm, "construction": true});
            skLineSegment(sketch, "E36.0.4.54", {"start": v(-12.98, 0.24) * mm, "end": v(12.98, 0.24) * mm, "construction": true});
            skLineSegment(sketch, "E36.0.4.55", {"start": v(-9.23, 6.74) * mm, "end": v(-5.48, 0.24) * mm});
            skLineSegment(sketch, "E36.0.5.0", {"start": v(-3.75, 29.22) * mm, "end": v(3.75, 29.22) * mm});
            skLineSegment(sketch, "E36.0.5.1", {"start": v(-7.5, 22.73) * mm, "end": v(-3.75, 29.22) * mm});
            skLineSegment(sketch, "E36.0.5.2", {"start": v(7.5, 22.73) * mm, "end": v(3.75, 16.23) * mm});
            skLineSegment(sketch, "E36.0.5.3", {"start": v(-20.48, 15.23) * mm, "end": v(-16.73, 21.73) * mm});
            skCircle(sketch, "E36.0.5.4", {"center": v(-25.96, 22.73) * mm, "radius": 7.5 * mm, "construction": true});
            skLineSegment(sketch, "E36.0.5.5", {"start": v(35.2, 21.73) * mm, "end": v(31.45, 15.23) * mm});
            skLineSegment(sketch, "E36.0.5.6", {"start": v(12.98, 15.23) * mm, "end": v(0, 22.73) * mm, "construction": true});
            skCircle(sketch, "E36.0.5.7", {"center": v(38.95, 15.23) * mm, "radius": 7.5 * mm, "construction": true});
            skLineSegment(sketch, "E36.0.5.8", {"start": v(-12.98, 15.23) * mm, "end": v(0, 22.73) * mm, "construction": true});
            skLineSegment(sketch, "E36.0.5.9", {"start": v(9.23, 21.73) * mm, "end": v(5.48, 15.23) * mm});
            skCircle(sketch, "E36.0.5.10", {"center": v(-38.95, 15.23) * mm, "radius": 7.5 * mm, "construction": true});
            skLineSegment(sketch, "E36.0.5.11", {"start": v(-5.48, 15.23) * mm, "end": v(-9.23, 8.74) * mm});
            skLineSegment(sketch, "E36.0.5.12", {"start": v(33.46, 22.73) * mm, "end": v(29.71, 16.23) * mm});
            skLineSegment(sketch, "E36.0.5.13", {"start": v(35.2, 8.74) * mm, "end": v(42.7, 8.74) * mm});
            skLineSegment(sketch, "E36.0.5.14", {"start": v(29.71, 16.23) * mm, "end": v(22.21, 16.23) * mm});
            skLineSegment(sketch, "E36.0.5.15", {"start": v(12.98, 15.23) * mm, "end": v(25.96, 22.73) * mm, "construction": true});
            skCircle(sketch, "E36.0.5.16", {"center": v(0, 22.73) * mm, "radius": 7.5 * mm, "construction": true});
            skCircle(sketch, "E36.0.5.17", {"center": v(-12.98, 15.23) * mm, "radius": 7.5 * mm, "construction": true});
            skLineSegment(sketch, "E36.0.5.18", {"start": v(-16.73, 21.73) * mm, "end": v(-9.23, 21.73) * mm});
            skLineSegment(sketch, "E36.0.5.19", {"start": v(-3.75, 16.23) * mm, "end": v(-7.5, 22.73) * mm});
            skLineSegment(sketch, "E36.0.5.20", {"start": v(3.75, 29.22) * mm, "end": v(7.5, 22.73) * mm});
            skLineSegment(sketch, "E36.0.5.21", {"start": v(-22.21, 16.23) * mm, "end": v(-18.46, 22.73) * mm});
            skLineSegment(sketch, "E36.0.5.22", {"start": v(-31.45, 15.23) * mm, "end": v(-35.2, 8.74) * mm});
            skLineSegment(sketch, "E36.0.5.23", {"start": v(16.73, 21.73) * mm, "end": v(9.23, 21.73) * mm});
            skLineSegment(sketch, "E36.0.5.24", {"start": v(29.71, 29.22) * mm, "end": v(33.46, 22.73) * mm});
            skLineSegment(sketch, "E36.0.5.25", {"start": v(46.45, 15.23) * mm, "end": v(42.7, 21.73) * mm});
            skLineSegment(sketch, "E36.0.5.26", {"start": v(42.7, 8.74) * mm, "end": v(46.45, 15.23) * mm});
            skLineSegment(sketch, "E36.0.5.27", {"start": v(5.48, 15.23) * mm, "end": v(9.23, 8.74) * mm});
            skLineSegment(sketch, "E36.0.5.28", {"start": v(-46.45, 15.23) * mm, "end": v(-42.7, 21.73) * mm});
            skLineSegment(sketch, "E36.0.5.29", {"start": v(31.45, 15.23) * mm, "end": v(35.2, 8.74) * mm});
            skLineSegment(sketch, "E36.0.5.30", {"start": v(16.73, 8.74) * mm, "end": v(20.48, 15.23) * mm});
            skLineSegment(sketch, "E36.0.5.31", {"start": v(-16.73, 8.74) * mm, "end": v(-20.48, 15.23) * mm});
            skLineSegment(sketch, "E36.0.5.32", {"start": v(-29.71, 16.23) * mm, "end": v(-22.21, 16.23) * mm});
            skLineSegment(sketch, "E36.0.5.33", {"start": v(20.48, 15.23) * mm, "end": v(16.73, 21.73) * mm});
            skLineSegment(sketch, "E36.0.5.34", {"start": v(-12.98, 15.23) * mm, "end": v(-25.96, 22.73) * mm, "construction": true});
            skLineSegment(sketch, "E36.0.5.35", {"start": v(-18.46, 22.73) * mm, "end": v(-22.21, 29.22) * mm});
            skLineSegment(sketch, "E36.0.5.36", {"start": v(42.7, 21.73) * mm, "end": v(35.2, 21.73) * mm});
            skLineSegment(sketch, "E36.0.5.37", {"start": v(-22.21, 29.22) * mm, "end": v(-29.71, 29.22) * mm});
            skLineSegment(sketch, "E36.0.5.38", {"start": v(-35.2, 21.73) * mm, "end": v(-31.45, 15.23) * mm});
            skLineSegment(sketch, "E36.0.5.39", {"start": v(-9.23, 8.74) * mm, "end": v(-16.73, 8.74) * mm});
            skLineSegment(sketch, "E36.0.5.40", {"start": v(22.21, 29.22) * mm, "end": v(29.71, 29.22) * mm});
            skLineSegment(sketch, "E36.0.5.41", {"start": v(22.21, 16.23) * mm, "end": v(18.46, 22.73) * mm});
            skLineSegment(sketch, "E36.0.5.42", {"start": v(3.75, 16.23) * mm, "end": v(-3.75, 16.23) * mm});
            skLineSegment(sketch, "E36.0.5.43", {"start": v(38.95, 15.23) * mm, "end": v(25.96, 22.73) * mm, "construction": true});
            skCircle(sketch, "E36.0.5.44", {"center": v(12.98, 15.23) * mm, "radius": 7.5 * mm, "construction": true});
            skLineSegment(sketch, "E36.0.5.45", {"start": v(-29.71, 29.22) * mm, "end": v(-33.46, 22.73) * mm});
            skCircle(sketch, "E36.0.5.46", {"center": v(25.96, 22.73) * mm, "radius": 7.5 * mm, "construction": true});
            skLineSegment(sketch, "E36.0.5.47", {"start": v(18.46, 22.73) * mm, "end": v(22.21, 29.22) * mm});
            skLineSegment(sketch, "E36.0.5.48", {"start": v(-35.2, 8.74) * mm, "end": v(-42.7, 8.74) * mm});
            skLineSegment(sketch, "E36.0.5.49", {"start": v(9.23, 8.74) * mm, "end": v(16.73, 8.74) * mm});
            skLineSegment(sketch, "E36.0.5.50", {"start": v(-33.46, 22.73) * mm, "end": v(-29.71, 16.23) * mm});
            skLineSegment(sketch, "E36.0.5.51", {"start": v(-42.7, 21.73) * mm, "end": v(-35.2, 21.73) * mm});
            skLineSegment(sketch, "E36.0.5.52", {"start": v(-42.7, 8.74) * mm, "end": v(-46.45, 15.23) * mm});
            skLineSegment(sketch, "E36.0.5.53", {"start": v(-38.95, 15.23) * mm, "end": v(-25.96, 22.73) * mm, "construction": true});
            skLineSegment(sketch, "E36.0.5.54", {"start": v(-12.98, 15.23) * mm, "end": v(12.98, 15.23) * mm, "construction": true});
            skLineSegment(sketch, "E36.0.5.55", {"start": v(-9.23, 21.73) * mm, "end": v(-5.48, 15.23) * mm});
            skLineSegment(sketch, "E36.0.6.0", {"start": v(-3.75, 44.21) * mm, "end": v(3.75, 44.21) * mm});
            skLineSegment(sketch, "E36.0.6.1", {"start": v(-7.5, 37.72) * mm, "end": v(-3.75, 44.21) * mm});
            skLineSegment(sketch, "E36.0.6.2", {"start": v(7.5, 37.72) * mm, "end": v(3.75, 31.22) * mm});
            skLineSegment(sketch, "E36.0.6.3", {"start": v(-20.48, 30.22) * mm, "end": v(-16.73, 36.72) * mm});
            skCircle(sketch, "E36.0.6.4", {"center": v(-25.96, 37.72) * mm, "radius": 7.5 * mm, "construction": true});
            skLineSegment(sketch, "E36.0.6.5", {"start": v(35.2, 36.72) * mm, "end": v(31.45, 30.22) * mm});
            skLineSegment(sketch, "E36.0.6.6", {"start": v(12.98, 30.22) * mm, "end": v(0, 37.72) * mm, "construction": true});
            skCircle(sketch, "E36.0.6.7", {"center": v(38.95, 30.22) * mm, "radius": 7.5 * mm, "construction": true});
            skLineSegment(sketch, "E36.0.6.8", {"start": v(-12.98, 30.22) * mm, "end": v(0, 37.72) * mm, "construction": true});
            skLineSegment(sketch, "E36.0.6.9", {"start": v(9.23, 36.72) * mm, "end": v(5.48, 30.22) * mm});
            skCircle(sketch, "E36.0.6.10", {"center": v(-38.95, 30.22) * mm, "radius": 7.5 * mm, "construction": true});
            skLineSegment(sketch, "E36.0.6.11", {"start": v(-5.48, 30.22) * mm, "end": v(-9.23, 23.73) * mm});
            skLineSegment(sketch, "E36.0.6.12", {"start": v(33.46, 37.72) * mm, "end": v(29.71, 31.22) * mm});
            skLineSegment(sketch, "E36.0.6.13", {"start": v(35.2, 23.73) * mm, "end": v(42.7, 23.73) * mm});
            skLineSegment(sketch, "E36.0.6.14", {"start": v(29.71, 31.22) * mm, "end": v(22.21, 31.22) * mm});
            skLineSegment(sketch, "E36.0.6.15", {"start": v(12.98, 30.22) * mm, "end": v(25.96, 37.72) * mm, "construction": true});
            skCircle(sketch, "E36.0.6.16", {"center": v(0, 37.72) * mm, "radius": 7.5 * mm, "construction": true});
            skCircle(sketch, "E36.0.6.17", {"center": v(-12.98, 30.22) * mm, "radius": 7.5 * mm, "construction": true});
            skLineSegment(sketch, "E36.0.6.18", {"start": v(-16.73, 36.72) * mm, "end": v(-9.23, 36.72) * mm});
            skLineSegment(sketch, "E36.0.6.19", {"start": v(-3.75, 31.22) * mm, "end": v(-7.5, 37.72) * mm});
            skLineSegment(sketch, "E36.0.6.20", {"start": v(3.75, 44.21) * mm, "end": v(7.5, 37.72) * mm});
            skLineSegment(sketch, "E36.0.6.21", {"start": v(-22.21, 31.22) * mm, "end": v(-18.46, 37.72) * mm});
            skLineSegment(sketch, "E36.0.6.22", {"start": v(-31.45, 30.22) * mm, "end": v(-35.2, 23.73) * mm});
            skLineSegment(sketch, "E36.0.6.23", {"start": v(16.73, 36.72) * mm, "end": v(9.23, 36.72) * mm});
            skLineSegment(sketch, "E36.0.6.24", {"start": v(29.71, 44.21) * mm, "end": v(33.46, 37.72) * mm});
            skLineSegment(sketch, "E36.0.6.25", {"start": v(46.45, 30.22) * mm, "end": v(42.7, 36.72) * mm});
            skLineSegment(sketch, "E36.0.6.26", {"start": v(42.7, 23.73) * mm, "end": v(46.45, 30.22) * mm});
            skLineSegment(sketch, "E36.0.6.27", {"start": v(5.48, 30.22) * mm, "end": v(9.23, 23.73) * mm});
            skLineSegment(sketch, "E36.0.6.28", {"start": v(-46.45, 30.22) * mm, "end": v(-42.7, 36.72) * mm});
            skLineSegment(sketch, "E36.0.6.29", {"start": v(31.45, 30.22) * mm, "end": v(35.2, 23.73) * mm});
            skLineSegment(sketch, "E36.0.6.30", {"start": v(16.73, 23.73) * mm, "end": v(20.48, 30.22) * mm});
            skLineSegment(sketch, "E36.0.6.31", {"start": v(-16.73, 23.73) * mm, "end": v(-20.48, 30.22) * mm});
            skLineSegment(sketch, "E36.0.6.32", {"start": v(-29.71, 31.22) * mm, "end": v(-22.21, 31.22) * mm});
            skLineSegment(sketch, "E36.0.6.33", {"start": v(20.48, 30.22) * mm, "end": v(16.73, 36.72) * mm});
            skLineSegment(sketch, "E36.0.6.34", {"start": v(-12.98, 30.22) * mm, "end": v(-25.96, 37.72) * mm, "construction": true});
            skLineSegment(sketch, "E36.0.6.35", {"start": v(-18.46, 37.72) * mm, "end": v(-22.21, 44.21) * mm});
            skLineSegment(sketch, "E36.0.6.36", {"start": v(42.7, 36.72) * mm, "end": v(35.2, 36.72) * mm});
            skLineSegment(sketch, "E36.0.6.37", {"start": v(-22.21, 44.21) * mm, "end": v(-29.71, 44.21) * mm});
            skLineSegment(sketch, "E36.0.6.38", {"start": v(-35.2, 36.72) * mm, "end": v(-31.45, 30.22) * mm});
            skLineSegment(sketch, "E36.0.6.39", {"start": v(-9.23, 23.73) * mm, "end": v(-16.73, 23.73) * mm});
            skLineSegment(sketch, "E36.0.6.40", {"start": v(22.21, 44.21) * mm, "end": v(29.71, 44.21) * mm});
            skLineSegment(sketch, "E36.0.6.41", {"start": v(22.21, 31.22) * mm, "end": v(18.46, 37.72) * mm});
            skLineSegment(sketch, "E36.0.6.42", {"start": v(3.75, 31.22) * mm, "end": v(-3.75, 31.22) * mm});
            skLineSegment(sketch, "E36.0.6.43", {"start": v(38.95, 30.22) * mm, "end": v(25.96, 37.72) * mm, "construction": true});
            skCircle(sketch, "E36.0.6.44", {"center": v(12.98, 30.22) * mm, "radius": 7.5 * mm, "construction": true});
            skLineSegment(sketch, "E36.0.6.45", {"start": v(-29.71, 44.21) * mm, "end": v(-33.46, 37.72) * mm});
            skCircle(sketch, "E36.0.6.46", {"center": v(25.96, 37.72) * mm, "radius": 7.5 * mm, "construction": true});
            skLineSegment(sketch, "E36.0.6.47", {"start": v(18.46, 37.72) * mm, "end": v(22.21, 44.21) * mm});
            skLineSegment(sketch, "E36.0.6.48", {"start": v(-35.2, 23.73) * mm, "end": v(-42.7, 23.73) * mm});
            skLineSegment(sketch, "E36.0.6.49", {"start": v(9.23, 23.73) * mm, "end": v(16.73, 23.73) * mm});
            skLineSegment(sketch, "E36.0.6.50", {"start": v(-33.46, 37.72) * mm, "end": v(-29.71, 31.22) * mm});
            skLineSegment(sketch, "E36.0.6.51", {"start": v(-42.7, 36.72) * mm, "end": v(-35.2, 36.72) * mm});
            skLineSegment(sketch, "E36.0.6.52", {"start": v(-42.7, 23.73) * mm, "end": v(-46.45, 30.22) * mm});
            skLineSegment(sketch, "E36.0.6.53", {"start": v(-38.95, 30.22) * mm, "end": v(-25.96, 37.72) * mm, "construction": true});
            skLineSegment(sketch, "E36.0.6.54", {"start": v(-12.98, 30.22) * mm, "end": v(12.98, 30.22) * mm, "construction": true});
            skLineSegment(sketch, "E36.0.6.55", {"start": v(-9.23, 36.72) * mm, "end": v(-5.48, 30.22) * mm});
            skLineSegment(sketch, "E36.0.7.0", {"start": v(-3.75, 59.2) * mm, "end": v(3.75, 59.2) * mm});
            skLineSegment(sketch, "E36.0.7.1", {"start": v(-7.5, 52.7) * mm, "end": v(-3.75, 59.2) * mm});
            skLineSegment(sketch, "E36.0.7.2", {"start": v(7.5, 52.7) * mm, "end": v(3.75, 46.21) * mm});
            skLineSegment(sketch, "E36.0.7.3", {"start": v(-20.48, 45.21) * mm, "end": v(-16.73, 51.7) * mm});
            skCircle(sketch, "E36.0.7.4", {"center": v(-25.96, 52.7) * mm, "radius": 7.5 * mm, "construction": true});
            skLineSegment(sketch, "E36.0.7.5", {"start": v(35.2, 51.7) * mm, "end": v(31.45, 45.21) * mm});
            skLineSegment(sketch, "E36.0.7.6", {"start": v(12.98, 45.21) * mm, "end": v(0, 52.7) * mm, "construction": true});
            skCircle(sketch, "E36.0.7.7", {"center": v(38.95, 45.21) * mm, "radius": 7.5 * mm, "construction": true});
            skLineSegment(sketch, "E36.0.7.8", {"start": v(-12.98, 45.21) * mm, "end": v(0, 52.7) * mm, "construction": true});
            skLineSegment(sketch, "E36.0.7.9", {"start": v(9.23, 51.7) * mm, "end": v(5.48, 45.21) * mm});
            skCircle(sketch, "E36.0.7.10", {"center": v(-38.95, 45.21) * mm, "radius": 7.5 * mm, "construction": true});
            skLineSegment(sketch, "E36.0.7.11", {"start": v(-5.48, 45.21) * mm, "end": v(-9.23, 38.72) * mm});
            skLineSegment(sketch, "E36.0.7.12", {"start": v(33.46, 52.7) * mm, "end": v(29.71, 46.21) * mm});
            skLineSegment(sketch, "E36.0.7.13", {"start": v(35.2, 38.72) * mm, "end": v(42.7, 38.72) * mm});
            skLineSegment(sketch, "E36.0.7.14", {"start": v(29.71, 46.21) * mm, "end": v(22.21, 46.21) * mm});
            skLineSegment(sketch, "E36.0.7.15", {"start": v(12.98, 45.21) * mm, "end": v(25.96, 52.7) * mm, "construction": true});
            skCircle(sketch, "E36.0.7.16", {"center": v(0, 52.7) * mm, "radius": 7.5 * mm, "construction": true});
            skCircle(sketch, "E36.0.7.17", {"center": v(-12.98, 45.21) * mm, "radius": 7.5 * mm, "construction": true});
            skLineSegment(sketch, "E36.0.7.18", {"start": v(-16.73, 51.7) * mm, "end": v(-9.23, 51.7) * mm});
            skLineSegment(sketch, "E36.0.7.19", {"start": v(-3.75, 46.21) * mm, "end": v(-7.5, 52.7) * mm});
            skLineSegment(sketch, "E36.0.7.20", {"start": v(3.75, 59.2) * mm, "end": v(7.5, 52.7) * mm});
            skLineSegment(sketch, "E36.0.7.21", {"start": v(-22.21, 46.21) * mm, "end": v(-18.46, 52.7) * mm});
            skLineSegment(sketch, "E36.0.7.22", {"start": v(-31.45, 45.21) * mm, "end": v(-35.2, 38.72) * mm});
            skLineSegment(sketch, "E36.0.7.23", {"start": v(16.73, 51.7) * mm, "end": v(9.23, 51.7) * mm});
            skLineSegment(sketch, "E36.0.7.24", {"start": v(29.71, 59.2) * mm, "end": v(33.46, 52.7) * mm});
            skLineSegment(sketch, "E36.0.7.25", {"start": v(46.45, 45.21) * mm, "end": v(42.7, 51.7) * mm});
            skLineSegment(sketch, "E36.0.7.26", {"start": v(42.7, 38.72) * mm, "end": v(46.45, 45.21) * mm});
            skLineSegment(sketch, "E36.0.7.27", {"start": v(5.48, 45.21) * mm, "end": v(9.23, 38.72) * mm});
            skLineSegment(sketch, "E36.0.7.28", {"start": v(-46.45, 45.21) * mm, "end": v(-42.7, 51.7) * mm});
            skLineSegment(sketch, "E36.0.7.29", {"start": v(31.45, 45.21) * mm, "end": v(35.2, 38.72) * mm});
            skLineSegment(sketch, "E36.0.7.30", {"start": v(16.73, 38.72) * mm, "end": v(20.48, 45.21) * mm});
            skLineSegment(sketch, "E36.0.7.31", {"start": v(-16.73, 38.72) * mm, "end": v(-20.48, 45.21) * mm});
            skLineSegment(sketch, "E36.0.7.32", {"start": v(-29.71, 46.21) * mm, "end": v(-22.21, 46.21) * mm});
            skLineSegment(sketch, "E36.0.7.33", {"start": v(20.48, 45.21) * mm, "end": v(16.73, 51.7) * mm});
            skLineSegment(sketch, "E36.0.7.34", {"start": v(-12.98, 45.21) * mm, "end": v(-25.96, 52.7) * mm, "construction": true});
            skLineSegment(sketch, "E36.0.7.35", {"start": v(-18.46, 52.7) * mm, "end": v(-22.21, 59.2) * mm});
            skLineSegment(sketch, "E36.0.7.36", {"start": v(42.7, 51.7) * mm, "end": v(35.2, 51.7) * mm});
            skLineSegment(sketch, "E36.0.7.37", {"start": v(-22.21, 59.2) * mm, "end": v(-29.71, 59.2) * mm});
            skLineSegment(sketch, "E36.0.7.38", {"start": v(-35.2, 51.7) * mm, "end": v(-31.45, 45.21) * mm});
            skLineSegment(sketch, "E36.0.7.39", {"start": v(-9.23, 38.72) * mm, "end": v(-16.73, 38.72) * mm});
            skLineSegment(sketch, "E36.0.7.40", {"start": v(22.21, 59.2) * mm, "end": v(29.71, 59.2) * mm});
            skLineSegment(sketch, "E36.0.7.41", {"start": v(22.21, 46.21) * mm, "end": v(18.46, 52.7) * mm});
            skLineSegment(sketch, "E36.0.7.42", {"start": v(3.75, 46.21) * mm, "end": v(-3.75, 46.21) * mm});
            skLineSegment(sketch, "E36.0.7.43", {"start": v(38.95, 45.21) * mm, "end": v(25.96, 52.7) * mm, "construction": true});
            skCircle(sketch, "E36.0.7.44", {"center": v(12.98, 45.21) * mm, "radius": 7.5 * mm, "construction": true});
            skLineSegment(sketch, "E36.0.7.45", {"start": v(-29.71, 59.2) * mm, "end": v(-33.46, 52.7) * mm});
            skCircle(sketch, "E36.0.7.46", {"center": v(25.96, 52.7) * mm, "radius": 7.5 * mm, "construction": true});
            skLineSegment(sketch, "E36.0.7.47", {"start": v(18.46, 52.7) * mm, "end": v(22.21, 59.2) * mm});
            skLineSegment(sketch, "E36.0.7.48", {"start": v(-35.2, 38.72) * mm, "end": v(-42.7, 38.72) * mm});
            skLineSegment(sketch, "E36.0.7.49", {"start": v(9.23, 38.72) * mm, "end": v(16.73, 38.72) * mm});
            skLineSegment(sketch, "E36.0.7.50", {"start": v(-33.46, 52.7) * mm, "end": v(-29.71, 46.21) * mm});
            skLineSegment(sketch, "E36.0.7.51", {"start": v(-42.7, 51.7) * mm, "end": v(-35.2, 51.7) * mm});
            skLineSegment(sketch, "E36.0.7.52", {"start": v(-42.7, 38.72) * mm, "end": v(-46.45, 45.21) * mm});
            skLineSegment(sketch, "E36.0.7.53", {"start": v(-38.95, 45.21) * mm, "end": v(-25.96, 52.7) * mm, "construction": true});
            skLineSegment(sketch, "E36.0.7.54", {"start": v(-12.98, 45.21) * mm, "end": v(12.98, 45.21) * mm, "construction": true});
            skLineSegment(sketch, "E36.0.7.55", {"start": v(-9.23, 51.7) * mm, "end": v(-5.48, 45.21) * mm});
            skLineSegment(sketch, "E36.0.8.0", {"start": v(-3.75, 74.2) * mm, "end": v(3.75, 74.2) * mm});
            skLineSegment(sketch, "E36.0.8.1", {"start": v(-7.5, 67.7) * mm, "end": v(-3.75, 74.2) * mm});
            skLineSegment(sketch, "E36.0.8.2", {"start": v(7.5, 67.7) * mm, "end": v(3.75, 61.2) * mm});
            skLineSegment(sketch, "E36.0.8.3", {"start": v(-20.48, 60.2) * mm, "end": v(-16.73, 66.7) * mm});
            skCircle(sketch, "E36.0.8.4", {"center": v(-25.96, 67.7) * mm, "radius": 7.5 * mm, "construction": true});
            skLineSegment(sketch, "E36.0.8.5", {"start": v(35.2, 66.7) * mm, "end": v(31.45, 60.2) * mm});
            skLineSegment(sketch, "E36.0.8.6", {"start": v(12.98, 60.2) * mm, "end": v(0, 67.7) * mm, "construction": true});
            skCircle(sketch, "E36.0.8.7", {"center": v(38.95, 60.2) * mm, "radius": 7.5 * mm, "construction": true});
            skLineSegment(sketch, "E36.0.8.8", {"start": v(-12.98, 60.2) * mm, "end": v(0, 67.7) * mm, "construction": true});
            skLineSegment(sketch, "E36.0.8.9", {"start": v(9.23, 66.7) * mm, "end": v(5.48, 60.2) * mm});
            skCircle(sketch, "E36.0.8.10", {"center": v(-38.95, 60.2) * mm, "radius": 7.5 * mm, "construction": true});
            skLineSegment(sketch, "E36.0.8.11", {"start": v(-5.48, 60.2) * mm, "end": v(-9.23, 53.7) * mm});
            skLineSegment(sketch, "E36.0.8.12", {"start": v(33.46, 67.7) * mm, "end": v(29.71, 61.2) * mm});
            skLineSegment(sketch, "E36.0.8.13", {"start": v(35.2, 53.7) * mm, "end": v(42.7, 53.7) * mm});
            skLineSegment(sketch, "E36.0.8.14", {"start": v(29.71, 61.2) * mm, "end": v(22.21, 61.2) * mm});
            skLineSegment(sketch, "E36.0.8.15", {"start": v(12.98, 60.2) * mm, "end": v(25.96, 67.7) * mm, "construction": true});
            skCircle(sketch, "E36.0.8.16", {"center": v(0, 67.7) * mm, "radius": 7.5 * mm, "construction": true});
            skCircle(sketch, "E36.0.8.17", {"center": v(-12.98, 60.2) * mm, "radius": 7.5 * mm, "construction": true});
            skLineSegment(sketch, "E36.0.8.18", {"start": v(-16.73, 66.7) * mm, "end": v(-9.23, 66.7) * mm});
            skLineSegment(sketch, "E36.0.8.19", {"start": v(-3.75, 61.2) * mm, "end": v(-7.5, 67.7) * mm});
            skLineSegment(sketch, "E36.0.8.20", {"start": v(3.75, 74.2) * mm, "end": v(7.5, 67.7) * mm});
            skLineSegment(sketch, "E36.0.8.21", {"start": v(-22.21, 61.2) * mm, "end": v(-18.46, 67.7) * mm});
            skLineSegment(sketch, "E36.0.8.22", {"start": v(-31.45, 60.2) * mm, "end": v(-35.2, 53.7) * mm});
            skLineSegment(sketch, "E36.0.8.23", {"start": v(16.73, 66.7) * mm, "end": v(9.23, 66.7) * mm});
            skLineSegment(sketch, "E36.0.8.24", {"start": v(29.71, 74.2) * mm, "end": v(33.46, 67.7) * mm});
            skLineSegment(sketch, "E36.0.8.25", {"start": v(46.45, 60.2) * mm, "end": v(42.7, 66.7) * mm});
            skLineSegment(sketch, "E36.0.8.26", {"start": v(42.7, 53.7) * mm, "end": v(46.45, 60.2) * mm});
            skLineSegment(sketch, "E36.0.8.27", {"start": v(5.48, 60.2) * mm, "end": v(9.23, 53.7) * mm});
            skLineSegment(sketch, "E36.0.8.28", {"start": v(-46.45, 60.2) * mm, "end": v(-42.7, 66.7) * mm});
            skLineSegment(sketch, "E36.0.8.29", {"start": v(31.45, 60.2) * mm, "end": v(35.2, 53.7) * mm});
            skLineSegment(sketch, "E36.0.8.30", {"start": v(16.73, 53.7) * mm, "end": v(20.48, 60.2) * mm});
            skLineSegment(sketch, "E36.0.8.31", {"start": v(-16.73, 53.7) * mm, "end": v(-20.48, 60.2) * mm});
            skLineSegment(sketch, "E36.0.8.32", {"start": v(-29.71, 61.2) * mm, "end": v(-22.21, 61.2) * mm});
            skLineSegment(sketch, "E36.0.8.33", {"start": v(20.48, 60.2) * mm, "end": v(16.73, 66.7) * mm});
            skLineSegment(sketch, "E36.0.8.34", {"start": v(-12.98, 60.2) * mm, "end": v(-25.96, 67.7) * mm, "construction": true});
            skLineSegment(sketch, "E36.0.8.35", {"start": v(-18.46, 67.7) * mm, "end": v(-22.21, 74.2) * mm});
            skLineSegment(sketch, "E36.0.8.36", {"start": v(42.7, 66.7) * mm, "end": v(35.2, 66.7) * mm});
            skLineSegment(sketch, "E36.0.8.37", {"start": v(-22.21, 74.2) * mm, "end": v(-29.71, 74.2) * mm});
            skLineSegment(sketch, "E36.0.8.38", {"start": v(-35.2, 66.7) * mm, "end": v(-31.45, 60.2) * mm});
            skLineSegment(sketch, "E36.0.8.39", {"start": v(-9.23, 53.7) * mm, "end": v(-16.73, 53.7) * mm});
            skLineSegment(sketch, "E36.0.8.40", {"start": v(22.21, 74.2) * mm, "end": v(29.71, 74.2) * mm});
            skLineSegment(sketch, "E36.0.8.41", {"start": v(22.21, 61.2) * mm, "end": v(18.46, 67.7) * mm});
            skLineSegment(sketch, "E36.0.8.42", {"start": v(3.75, 61.2) * mm, "end": v(-3.75, 61.2) * mm});
            skLineSegment(sketch, "E36.0.8.43", {"start": v(38.95, 60.2) * mm, "end": v(25.96, 67.7) * mm, "construction": true});
            skCircle(sketch, "E36.0.8.44", {"center": v(12.98, 60.2) * mm, "radius": 7.5 * mm, "construction": true});
            skLineSegment(sketch, "E36.0.8.45", {"start": v(-29.71, 74.2) * mm, "end": v(-33.46, 67.7) * mm});
            skCircle(sketch, "E36.0.8.46", {"center": v(25.96, 67.7) * mm, "radius": 7.5 * mm, "construction": true});
            skLineSegment(sketch, "E36.0.8.47", {"start": v(18.46, 67.7) * mm, "end": v(22.21, 74.2) * mm});
            skLineSegment(sketch, "E36.0.8.48", {"start": v(-35.2, 53.7) * mm, "end": v(-42.7, 53.7) * mm});
            skLineSegment(sketch, "E36.0.8.49", {"start": v(9.23, 53.7) * mm, "end": v(16.73, 53.7) * mm});
            skLineSegment(sketch, "E36.0.8.50", {"start": v(-33.46, 67.7) * mm, "end": v(-29.71, 61.2) * mm});
            skLineSegment(sketch, "E36.0.8.51", {"start": v(-42.7, 66.7) * mm, "end": v(-35.2, 66.7) * mm});
            skLineSegment(sketch, "E36.0.8.52", {"start": v(-42.7, 53.7) * mm, "end": v(-46.45, 60.2) * mm});
            skLineSegment(sketch, "E36.0.8.53", {"start": v(-38.95, 60.2) * mm, "end": v(-25.96, 67.7) * mm, "construction": true});
            skLineSegment(sketch, "E36.0.8.54", {"start": v(-12.98, 60.2) * mm, "end": v(12.98, 60.2) * mm, "construction": true});
            skLineSegment(sketch, "E36.0.8.55", {"start": v(-9.23, 66.7) * mm, "end": v(-5.48, 60.2) * mm});
            skLineSegment(sketch, "E36.direction1", {"start": v(-42.7, -66.21) * mm, "end": v(-40, -66.21) * mm, "construction": true});
            skLineSegment(sketch, "E36.direction2", {"start": v(-42.7, -66.21) * mm, "end": v(-42.7, -51.22) * mm, "construction": true});
            skSolve(sketch);
        }
        {
            var Q0;
            Q0 = qSketchRegion(id + "F2", true);
            extrude(context, id + "F3", {"entities" : qUnion([Q0]), "operationType" : NewBodyOperationType.REMOVE, "offsetDistance" : 25 * mm, "depth" : 25 * mm});
        }
    });
